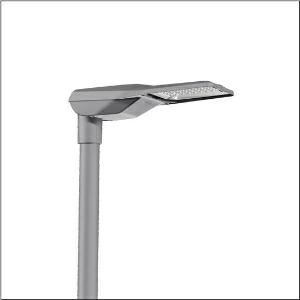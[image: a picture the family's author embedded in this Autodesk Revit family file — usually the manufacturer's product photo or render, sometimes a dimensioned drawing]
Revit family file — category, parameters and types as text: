
# Revit family: streetlight_sl_21_mini___p1_0a_5xe6a43a08gb_8ec3
name_source: partatom
category: Lighting Fixtures
units: mm (PartAtom-declared; Revit-internal decimal feet)

## family parameters
Cut with Voids When Loaded = No
Host = Face
Light Source = No
Part Type = Normal
Room Calculation Point = No
Round Connector Dimension = Use Diameter
Shared = No

## types (1)
- --- (1 x LED, 6180 lm, 40.4 W, 4000K)
    Apparent Load = 40 VA
    CIE Flux Codes = 21 50 90 100 100
    Color Rendering = 70
    Color Temperature = 4000K
    Default Elevation = 1800 mm
    Description = Streetlight SL 21 mini, mast luminaire, primary light control with lens, of PMMA, primary optical cover: cover, of toughened safety glass, transparent, light distribution: P1.0a, light emission: direct distribution, primary light characteristic: asymmetric, installation type: post-top, side-entry, LED, 3G 1.5mm², High Power LED, rated luminous flux: 6.180lm, luminous efficacy: 153lm/W, light colour: 740, colour temperature: 4000K, control: overheat protection, constant luminous flux control, time-dependent luminous flux control, flexible luminous flux parameterisation, mains connection: 230..240V, AC, 50/60Hz, connection cable pre-assembled, cable length: 6,5m, wiring characteristics: H07RN-F, start of lifetime: 40W, end of service life: 41W, reduction: 19W, luminaire housing, of diecast aluminium, powder-coated, Siteco® metallic grey (DB 702S), corrosivity category C5 mid according to DIN EN ISO 12944, please order mast flange separately, inclination adjustable: 0°, 5°, 10°, 15°, sealing non-destructively replaceable, multi-level sealing system, length: 628mm, width: 235mm, height: 110mm, mast flange for spigot size: 42mm (side-entry): 5XC10008XM4, 60/48mm (side-entry/post-top): 5XC10108XM2, 76/60mm (side-entry/post-top): 5XC10108XM1, protection rating (complete): IP66, insulation class (complete): insulation class II (safety insulation), certification: CE, ENEC, ENEC+, VDE, impact resistance: IK09, permissible operating ambient temperature for outdoor applications: -40..+50°C, standard-compliant lighting for roads and squares, packaging unit: 1 piece

Light Distribution: P1.0a
    Height = 110 mm
    Lamp = 1 x LED
    Lamp Light Flux = 6180 lm
    Lamp Power = 40.4 W
    Lamp count = 1
    Length = 625 mm
    Luminous efficacy = 153 lm/W
    Manufacturer = Siteco
    ModVariant = No
    Model = 5XE6A43A08GB
    Number of Poles = 1
    OnlyDefault = Yes
    Power Factor = 1
    Product Name = Streetlight SL 21 mini | P1.0a
    Product group = mast luminaire | pylon top
    ProductGroupID = 6100
    Protection Class = Protection class II
    Protection Degree = IP 66
    RLX_Detail_Level = 1
    RLX_Emergency_Light_Flux = 0 lm
    RLX_Emergency_Type = 0
    RLX_Emergency_Type_DB = No
    RlxData = <blob elided: 103345 chars, md5=0b61905d>
    Socket = socket
    Standby Power = 0 W
    System Light Flux = 6180 lm
    System Power = 40 W
    Type Comments = factory setting: luminous flux: 100 % | Output Level: 100 % | 812 mA
    Type Image = l_1003519.jpg
    URL = http://relux.com
    VarID = @adj_119869
    Voltage = 0 V
    Weight = 0.00 kg
    Width = 234 mm

## geometry (parser evidence)
native form markers: Blend x4, Sweep x11
no freeform markers — native parametric forms only
